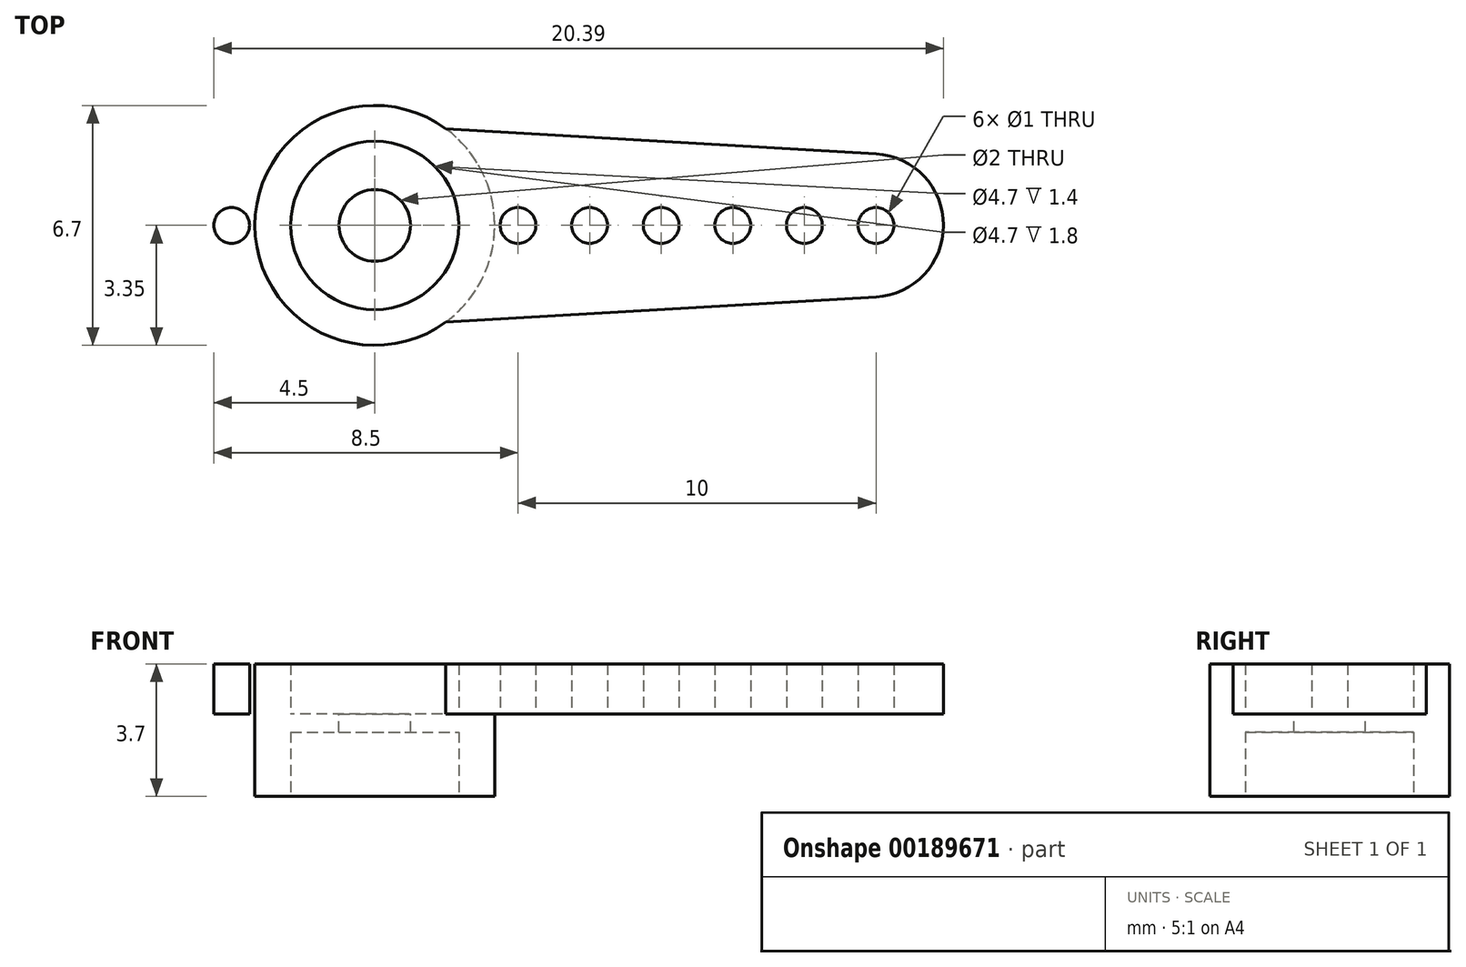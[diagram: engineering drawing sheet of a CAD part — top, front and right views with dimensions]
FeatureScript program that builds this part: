
annotation { "Feature Type Name" : "Feature", "Feature Type Description" : "" }
export const myFeature = defineFeature(function(context is Context, id is Id, definition is map)
    precondition{}
    {
        {
            var Q0;
            Q0=qCreatedBy(makeId("Top.planeOp"),FACE);
            var sketch = newSketch(context, id + "F0", { "sketchPlane" : qUnion([Q0])});
            skCircle(sketch, "E0", {"center": v(0, 0) * mm, "radius": 3.35 * mm});
            skCircle(sketch, "E1", {"center": v(6, 0) * mm, "radius": 0.5 * mm});
            skCircle(sketch, "E2.1.0.0", {"center": v(8, 0) * mm, "radius": 0.5 * mm});
            skCircle(sketch, "E2.2.0.0", {"center": v(10, 0) * mm, "radius": 0.5 * mm});
            skCircle(sketch, "E2.3.0.0", {"center": v(12, 0) * mm, "radius": 0.5 * mm});
            skCircle(sketch, "E2.4.0.0", {"center": v(14, 0) * mm, "radius": 0.5 * mm});
            skLineSegment(sketch, "E2.direction1", {"start": v(6, 0) * mm, "end": v(8, 0) * mm, "construction": true});
            skCircle(sketch, "E3.1.0.0", {"center": v(4, 0) * mm, "radius": 0.5 * mm});
            skLineSegment(sketch, "E3.direction1", {"start": v(6, 0) * mm, "end": v(4, 0) * mm, "construction": true});
            skCircle(sketch, "E4.0", {"center": v(0, 0) * mm, "radius": 2.35 * mm});
            skLineSegment(sketch, "E5", {"start": v(1.98, -2.7) * mm, "end": v(1.98, 2.7) * mm, "construction": true});
            skLineSegment(sketch, "E6", {"start": v(1.98, 2.7) * mm, "end": v(14, 2) * mm});
            skLineSegment(sketch, "E7.MirrorCS", {"start": v(1.98, -2.7) * mm, "end": v(14, -2) * mm});
            skArc(sketch, "E8", {"start": v(14, 2) * mm, "mid": v(15.89, 0) * mm, "end": v(14, -2) * mm});
            skLineSegment(sketch, "E9", {"start": v(0, 0) * mm, "end": v(0, 0.74) * mm, "construction": true});
            skCircle(sketch, "E10.MirrorC", {"center": v(-4, 0) * mm, "radius": 0.5 * mm});
            skCircle(sketch, "E11.MirrorC", {"center": v(-6, 0) * mm, "radius": 0.5 * mm});
            skLineSegment(sketch, "E12.MirrorCS", {"start": v(-1.98, 2.7) * mm, "end": v(-7, 2.4) * mm});
            skLineSegment(sketch, "E13.MirrorCS", {"start": v(-1.98, -2.7) * mm, "end": v(-7, -2.4) * mm});
            skLineSegment(sketch, "E14", {"start": v(-7, 2.4) * mm, "end": v(-7, -2.4) * mm});
            skPoint(sketch, "E15.orphan", {"position": v(-14, 2) * mm});
            skPoint(sketch, "E16.orphan", {"position": v(-14, -2) * mm});
            skSolve(sketch);
        }
        {
            var Q0;
            Q0=makeQuery(id+"F0.imprint","IMPRINT",FACE,{"disambiguationData":[TD([[makeQuery(id+"F0.imprint","IMPRINT",EDGE,{"derivedFrom":sQuery(id+"F0.wireOp",EDGE,"E4.0")}),-1.0]])]});
            var Q1;
            Q1=makeQuery(id+"F0.imprint","IMPRINT",FACE,{"disambiguationData":[TD([[makeQuery(id+"F0.imprint","IMPRINT",EDGE,{"derivedFrom":sQuery(id+"F0.wireOp",EDGE,"E1")}),-1.0]])]});
            var Q2;
            Q2=makeQuery(id+"F0.imprint","IMPRINT",FACE,{"disambiguationData":[TD([[makeQuery(id+"F0.imprint","IMPRINT",EDGE,{"derivedFrom":sQuery(id+"F0.wireOp",EDGE,"E10.MirrorC")}),1.0]])]});
            extrude(context, id + "F1", {"entities" : qUnion([Q0, Q1, Q2]), "depth" : 1.4 * mm});
        }
        {
            var Q0;
            Q0=makeQuery(id+"F1.opExtrude","CAP_FACE",FACE,{"disambiguationData":[OSD([sQuery(id+"F0.wireOp",EDGE,"E0"),sQuery(id+"F0.wireOp",EDGE,"E1"),sQuery(id+"F0.wireOp",EDGE,"E2.1.0.0"),sQuery(id+"F0.wireOp",EDGE,"E2.2.0.0"),sQuery(id+"F0.wireOp",EDGE,"E2.3.0.0"),sQuery(id+"F0.wireOp",EDGE,"E2.4.0.0"),sQuery(id+"F0.wireOp",EDGE,"E3.1.0.0"),sQuery(id+"F0.wireOp",EDGE,"E4.0"),sQuery(id+"F0.wireOp",EDGE,"E6"),sQuery(id+"F0.wireOp",EDGE,"E7.MirrorCS"),sQuery(id+"F0.wireOp",EDGE,"E8")])],"isStart":true});
            var sketch = newSketch(context, id + "F2", { "sketchPlane" : qUnion([Q0])});
            skLineSegment(sketch, "E17.0", {"start": v(1.98, -2.7) * mm, "end": v(1.98, -2.7) * mm});
            skCircle(sketch, "E18", {"center": v(0, 0) * mm, "radius": 3.35 * mm});
            skCircle(sketch, "E19", {"center": v(0, 0) * mm, "radius": 1 * mm});
            skSolve(sketch);
        }
        {
            var Q0;
            Q0=makeQuery(id+"F2.imprint","IMPRINT",FACE,{"disambiguationData":[TD([[makeQuery(id+"F2.imprint","IMPRINT",EDGE,{"derivedFrom":sQuery(id+"F2.wireOp",EDGE,"E19")}),-1.0]])]});
            var Q1;
            {var subQ0=sQuery(id+"F2.wireOp",EDGE,"E18");Q1=makeQuery(id+"F2.imprint","IMPRINT",FACE,{"disambiguationData":[TD([[makeQuery(id+"F2.imprint","IMPRINT",EDGE,{"disambiguationData":[OD(0.0)],"derivedFrom":subQ0}),-1.0]])]});}
            extrude(context, id + "F3", {"entities" : qUnion([Q0, Q1]), "operationType" : NewBodyOperationType.ADD, "depth" : 2.3 * mm});
        }
        {
            var Q0;
            Q0=makeQuery(id+"F3.opExtrude","CAP_FACE",FACE,{"disambiguationData":[OSD([sQuery(id+"F2.wireOp",EDGE,"E18"),sQuery(id+"F2.wireOp",EDGE,"E19")])],"isStart":false});
            var sketch = newSketch(context, id + "F4", { "sketchPlane" : qUnion([Q0])});
            skCircle(sketch, "E20.0", {"center": v(0, 0) * mm, "radius": 3.35 * mm, "construction": true});
            skCircle(sketch, "E21.0", {"center": v(0, 0) * mm, "radius": 2.35 * mm});
            skSolve(sketch);
        }
        {
            var Q0;
            Q0=makeQuery(id+"F4.imprint","IMPRINT",FACE,{"disambiguationData":[TD([[makeQuery(id+"F4.imprint","IMPRINT",EDGE,{"derivedFrom":sQuery(id+"F4.wireOp",EDGE,"E21.0")}),1.0]])]});
            extrude(context, id + "F5", {"entities" : qUnion([Q0]), "operationType" : NewBodyOperationType.REMOVE, "oppositeDirection" : true, "depth" : 1.8 * mm});
        }
    });
